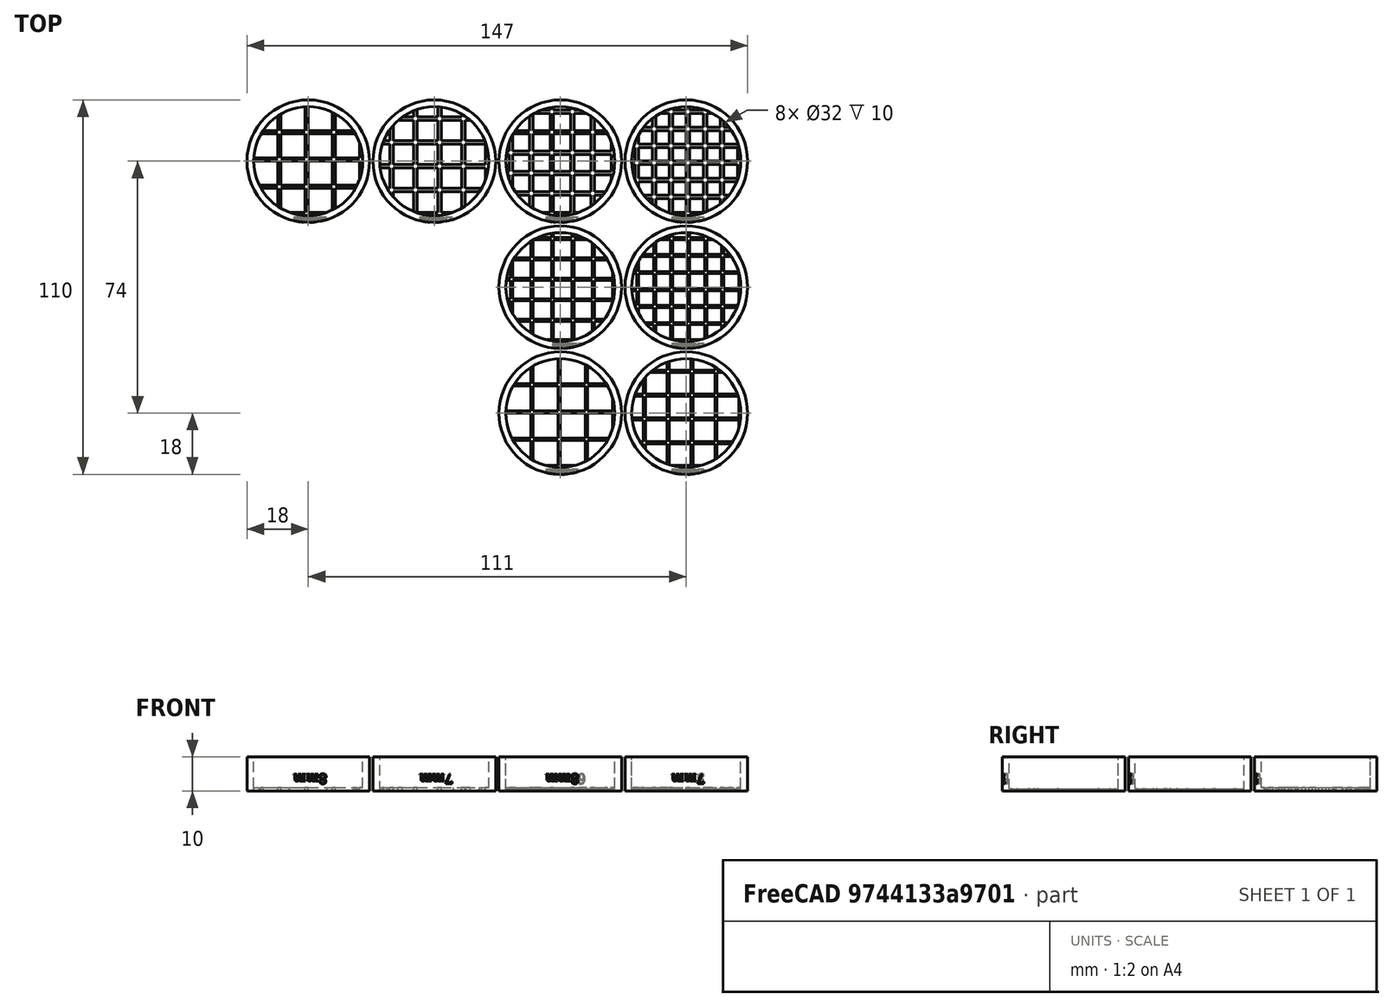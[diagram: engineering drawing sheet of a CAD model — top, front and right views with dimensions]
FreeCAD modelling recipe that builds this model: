
FCSTD DOCUMENT  (FreeCAD 0.18.4R)
Label: markingpots
License: All rights reserved
LicenseURL: http://en.wikipedia.org/wiki/All_rights_reserved
objects: Part::FeaturePython×16, Part::Cylinder×16, Part::Cut×16, Part::MultiFuse×16, Part::Box×8, Part::MultiCommon×8, Part::Part2DObjectPython×8, Part::Extrusion×8
note: 96 computed .brp shape members not serialized (recipe doc carries the construction recipe); baked Part::Feature solids carry a one-line shape summary decoded from their .brp

FEATURE [Part::Box] Box  label="Cube"
  AttacherType = Attacher::AttachEngine3D
  Height = 1
  Length = 32
  Width = 1
FEATURE [Part::FeaturePython] Array  # Draft array (typed FeaturePython)
  Angle = 360
  ArrayType = 0
  Axis = (0,0,1)
  Base = -> Box
  Center = (0,0,0)
  Fuse = false
  IntervalAxis = (0,0,0)
  IntervalX = (1,0,0)
  IntervalY = (0,5,0)
  IntervalZ = (0,0,1)
  NumberPolar = 1
  NumberX = 1
  NumberY = 7
  NumberZ = 1
FEATURE [Part::FeaturePython] Array001  # Draft array (typed FeaturePython)
  Angle = 90
  ArrayType = 1
  Axis = (0,0,1)
  Base = -> Array
  Center = (16,16,0)
  Fuse = false
  IntervalAxis = (0,0,0)
  IntervalX = (1,0,0)
  IntervalY = (0,1,0)
  IntervalZ = (0,0,1)
  NumberPolar = 2
  NumberX = 1
  NumberY = 1
  NumberZ = 1
FEATURE [Part::Cylinder] Cylinder
  Angle = 360
  AttacherType = Attacher::AttachEngine3D
  Height = 10
  Placement = pos=(16,16,0) rot=(0,0,1;0rad)
  Radius = 18
FEATURE [Part::Cylinder] Cylinder001
  Angle = 360
  AttacherType = Attacher::AttachEngine3D
  Height = 10
  Placement = pos=(16,16,0) rot=(0,0,1;0rad)
  Radius = 16
FEATURE [Part::Cut] Cut
  Base = -> Cylinder
  Tool = -> Cylinder001
FEATURE [Part::MultiFuse] Fusion
  Shapes = -> [Array001]
FEATURE [Part::MultiCommon] Common
  Shapes = -> [Cylinder,Fusion]
FEATURE [Part::MultiFuse] Fusion001
  Shapes = -> [Cut,Common]
FEATURE [Part::Part2DObjectPython] ShapeString  # Draft 2D object (typed FeaturePython)
  FontFile = <path>
  Placement = pos=(0,0,0) rot=(0,0,1;3.14159rad)
  Size = 3
  String = 5mm
  Tracking = 0
FEATURE [Part::Extrusion] Extrude
  Base = -> ShapeString
  Dir = (0,0,1)
  DirMode = 2
  FaceMakerClass = Part::FaceMakerBullseye
  LengthFwd = 2
  LengthRev = 0
  Placement = pos=(21.5,-0.5,5) rot=(1,0,0;1.5708rad)
  Solid = false
  Symmetric = false
FEATURE [Part::Cut] Cut001  label="5mm"
  Base = -> Fusion001
  Tool = -> Extrude
FEATURE [Part::Box] Box001  label="Cube001"
  AttacherType = Attacher::AttachEngine3D
  Height = 1
  Length = 32
  Width = 1
FEATURE [Part::FeaturePython] Array002  # Draft array (typed FeaturePython)
  Angle = 360
  ArrayType = 0
  Axis = (0,0,1)
  Base = -> Box001
  Center = (0,0,0)
  Fuse = false
  IntervalAxis = (0,0,0)
  IntervalX = (1,0,0)
  IntervalY = (0,6,0)
  IntervalZ = (0,0,1)
  NumberPolar = 1
  NumberX = 1
  NumberY = 7
  NumberZ = 1
FEATURE [Part::FeaturePython] Array003  # Draft array (typed FeaturePython)
  Angle = 90
  ArrayType = 1
  Axis = (0,0,1)
  Base = -> Array002
  Center = (16,16,0)
  Fuse = false
  IntervalAxis = (0,0,0)
  IntervalX = (1,0,0)
  IntervalY = (0,1,0)
  IntervalZ = (0,0,1)
  NumberPolar = 2
  NumberX = 1
  NumberY = 1
  NumberZ = 1
FEATURE [Part::Cylinder] Cylinder002
  Angle = 360
  AttacherType = Attacher::AttachEngine3D
  Height = 10
  Placement = pos=(16,16,0) rot=(0,0,1;0rad)
  Radius = 16
FEATURE [Part::MultiFuse] Fusion002
  Shapes = -> [Array003]
FEATURE [Part::Cylinder] Cylinder003
  Angle = 360
  AttacherType = Attacher::AttachEngine3D
  Height = 10
  Placement = pos=(16,16,0) rot=(0,0,1;0rad)
  Radius = 18
FEATURE [Part::MultiCommon] Common001
  Shapes = -> [Cylinder003,Fusion002]
FEATURE [Part::Cut] Cut002
  Base = -> Cylinder003
  Tool = -> Cylinder002
FEATURE [Part::MultiFuse] Fusion003
  Shapes = -> [Cut002,Common001]
FEATURE [Part::Part2DObjectPython] ShapeString001  # Draft 2D object (typed FeaturePython)
  FontFile = <path>
  Placement = pos=(0,0,0) rot=(0,0,1;3.14159rad)
  Size = 3
  String = 6mm
  Tracking = 0
FEATURE [Part::Extrusion] Extrude001
  Base = -> ShapeString001
  Dir = (0,0,1)
  DirMode = 2
  FaceMakerClass = Part::FaceMakerBullseye
  LengthFwd = 2
  LengthRev = 0
  Placement = pos=(21.5,-0.5,5) rot=(1,0,0;1.5708rad)
  Solid = false
  Symmetric = false
FEATURE [Part::Cut] Cut003  label="6mm"
  Base = -> Fusion003
  Placement = pos=(-37,0,0) rot=(0,0,1;0rad)
  Tool = -> Extrude001
FEATURE [Part::Box] Box002  label="Cube002"
  AttacherType = Attacher::AttachEngine3D
  Height = 0.6
  Length = 32
  Width = 0.6
FEATURE [Part::FeaturePython] Array004  # Draft array (typed FeaturePython)
  Angle = 360
  ArrayType = 0
  Axis = (0,0,1)
  Base = -> Box002
  Center = (0,0,0)
  Fuse = false
  IntervalAxis = (0,0,0)
  IntervalX = (1,0,0)
  IntervalY = (0,5,0)
  IntervalZ = (0,0,1)
  NumberPolar = 1
  NumberX = 1
  NumberY = 7
  NumberZ = 1
FEATURE [Part::FeaturePython] Array005  # Draft array (typed FeaturePython)
  Angle = 90
  ArrayType = 1
  Axis = (0,0,1)
  Base = -> Array004
  Center = (16,16,0)
  Fuse = false
  IntervalAxis = (0,0,0)
  IntervalX = (1,0,0)
  IntervalY = (0,1,0)
  IntervalZ = (0,0,1)
  NumberPolar = 2
  NumberX = 1
  NumberY = 1
  NumberZ = 1
FEATURE [Part::Cylinder] Cylinder004
  Angle = 360
  AttacherType = Attacher::AttachEngine3D
  Height = 10
  Placement = pos=(16,16,0) rot=(0,0,1;0rad)
  Radius = 16
FEATURE [Part::MultiFuse] Fusion004
  Shapes = -> [Array005]
FEATURE [Part::Cylinder] Cylinder005
  Angle = 360
  AttacherType = Attacher::AttachEngine3D
  Height = 10
  Placement = pos=(16,16,0) rot=(0,0,1;0rad)
  Radius = 18
FEATURE [Part::MultiCommon] Common002
  Shapes = -> [Cylinder005,Fusion004]
FEATURE [Part::Cut] Cut004
  Base = -> Cylinder005
  Tool = -> Cylinder004
FEATURE [Part::MultiFuse] Fusion005
  Shapes = -> [Cut004,Common002]
FEATURE [Part::Part2DObjectPython] ShapeString002  # Draft 2D object (typed FeaturePython)
  FontFile = <path>
  Placement = pos=(0,0,0) rot=(0,0,1;3.14159rad)
  Size = 3
  String = 5mm
  Tracking = 0
FEATURE [Part::Extrusion] Extrude002
  Base = -> ShapeString002
  Dir = (0,0,1)
  DirMode = 2
  FaceMakerClass = Part::FaceMakerBullseye
  LengthFwd = 2
  LengthRev = 0
  Placement = pos=(21.5,-0.5,5) rot=(1,0,0;1.5708rad)
  Solid = false
  Symmetric = false
FEATURE [Part::Cut] Cut005  label="5mm001"
  Base = -> Fusion005
  Placement = pos=(0,-37,0) rot=(0,0,1;0rad)
  Tool = -> Extrude002
FEATURE [Part::Part2DObjectPython] ShapeString003  # Draft 2D object (typed FeaturePython)
  FontFile = <path>
  Placement = pos=(0,0,0) rot=(0,0,1;3.14159rad)
  Size = 3
  String = 6mm
  Tracking = 0
FEATURE [Part::Cylinder] Cylinder006
  Angle = 360
  AttacherType = Attacher::AttachEngine3D
  Height = 10
  Placement = pos=(16,16,0) rot=(0,0,1;0rad)
  Radius = 16
FEATURE [Part::Cylinder] Cylinder007
  Angle = 360
  AttacherType = Attacher::AttachEngine3D
  Height = 10
  Placement = pos=(16,16,0) rot=(0,0,1;0rad)
  Radius = 18
FEATURE [Part::Box] Box003  label="Cube003"
  AttacherType = Attacher::AttachEngine3D
  Height = 0.6
  Length = 32
  Width = 0.6
FEATURE [Part::Extrusion] Extrude003
  Base = -> ShapeString003
  Dir = (0,0,1)
  DirMode = 2
  FaceMakerClass = Part::FaceMakerBullseye
  LengthFwd = 2
  LengthRev = 0
  Placement = pos=(23.5,-0.5,5) rot=(1,0,0;1.5708rad)
  Solid = false
  Symmetric = false
FEATURE [Part::Cut] Cut007
  Base = -> Cylinder007
  Tool = -> Cylinder006
FEATURE [Part::FeaturePython] Array007  # Draft array (typed FeaturePython)
  Angle = 360
  ArrayType = 0
  Axis = (0,0,1)
  Base = -> Box003
  Center = (0,0,0)
  Fuse = false
  IntervalAxis = (0,0,0)
  IntervalX = (1,0,0)
  IntervalY = (0,6,0)
  IntervalZ = (0,0,1)
  NumberPolar = 1
  NumberX = 1
  NumberY = 7
  NumberZ = 1
FEATURE [Part::FeaturePython] Array006  # Draft array (typed FeaturePython)
  Angle = 90
  ArrayType = 1
  Axis = (0,0,1)
  Base = -> Array007
  Center = (16,16,0)
  Fuse = false
  IntervalAxis = (0,0,0)
  IntervalX = (1,0,0)
  IntervalY = (0,1,0)
  IntervalZ = (0,0,1)
  NumberPolar = 2
  NumberX = 1
  NumberY = 1
  NumberZ = 1
FEATURE [Part::MultiFuse] Fusion007
  Shapes = -> [Array006]
FEATURE [Part::MultiCommon] Common003
  Shapes = -> [Cylinder007,Fusion007]
FEATURE [Part::MultiFuse] Fusion006
  Shapes = -> [Cut007,Common003]
FEATURE [Part::Cut] Cut006  label="6mm001"
  Base = -> Fusion006
  Placement = pos=(-37,-37,0) rot=(0,0,1;0rad)
  Tool = -> Extrude003
FEATURE [Part::Part2DObjectPython] ShapeString004  # Draft 2D object (typed FeaturePython)
  FontFile = <path>
  Placement = pos=(0,0,0) rot=(0,0,1;3.14159rad)
  Size = 3
  String = 7mm
  Tracking = 0
FEATURE [Part::Cylinder] Cylinder008
  Angle = 360
  AttacherType = Attacher::AttachEngine3D
  Height = 10
  Placement = pos=(16,16,0) rot=(0,0,1;0rad)
  Radius = 16
FEATURE [Part::Cylinder] Cylinder009
  Angle = 360
  AttacherType = Attacher::AttachEngine3D
  Height = 10
  Placement = pos=(16,16,0) rot=(0,0,1;0rad)
  Radius = 18
FEATURE [Part::Box] Box004  label="Cube004"
  AttacherType = Attacher::AttachEngine3D
  Height = 1
  Length = 32
  Width = 1
FEATURE [Part::Extrusion] Extrude004
  Base = -> ShapeString004
  Dir = (0,0,1)
  DirMode = 2
  FaceMakerClass = Part::FaceMakerBullseye
  LengthFwd = 2
  LengthRev = 0
  Placement = pos=(21.5,-0.5,5) rot=(1,0,0;1.5708rad)
  Solid = false
  Symmetric = false
FEATURE [Part::Cut] Cut011
  Base = -> Cylinder009
  Tool = -> Cylinder008
FEATURE [Part::FeaturePython] Array011  # Draft array (typed FeaturePython)
  Angle = 360
  ArrayType = 0
  Axis = (0,0,1)
  Base = -> Box004
  Center = (0,0,0)
  Fuse = false
  IntervalAxis = (0,0,0)
  IntervalX = (1,0,0)
  IntervalY = (0,7,0)
  IntervalZ = (0,0,1)
  NumberPolar = 1
  NumberX = 1
  NumberY = 7
  NumberZ = 1
FEATURE [Part::FeaturePython] Array008  # Draft array (typed FeaturePython)
  Angle = 90
  ArrayType = 1
  Axis = (0,0,1)
  Base = -> Array011
  Center = (16,16,0)
  Fuse = false
  IntervalAxis = (0,0,0)
  IntervalX = (1,0,0)
  IntervalY = (0,1,0)
  IntervalZ = (0,0,1)
  NumberPolar = 2
  NumberX = 1
  NumberY = 1
  NumberZ = 1
FEATURE [Part::MultiFuse] Fusion011
  Shapes = -> [Array008]
FEATURE [Part::MultiCommon] Common004
  Shapes = -> [Cylinder009,Fusion011]
FEATURE [Part::MultiFuse] Fusion009
  Shapes = -> [Cut011,Common004]
FEATURE [Part::Cut] Cut008  label="7mm"
  Base = -> Fusion009
  Placement = pos=(-74,0,0) rot=(0,0,1;0rad)
  Tool = -> Extrude004
FEATURE [Part::Part2DObjectPython] ShapeString005  # Draft 2D object (typed FeaturePython)
  FontFile = <path>
  Placement = pos=(0,0,0) rot=(0,0,1;3.14159rad)
  Size = 3
  String = 7mm
  Tracking = 0
FEATURE [Part::Extrusion] Extrude005
  Base = -> ShapeString005
  Dir = (0,0,1)
  DirMode = 2
  FaceMakerClass = Part::FaceMakerBullseye
  LengthFwd = 2
  LengthRev = 0
  Placement = pos=(21.5,-0.5,5) rot=(1,0,0;1.5708rad)
  Solid = false
  Symmetric = false
FEATURE [Part::Cylinder] Cylinder010
  Angle = 360
  AttacherType = Attacher::AttachEngine3D
  Height = 10
  Placement = pos=(16,16,0) rot=(0,0,1;0rad)
  Radius = 16
FEATURE [Part::Box] Box005  label="Cube005"
  AttacherType = Attacher::AttachEngine3D
  Height = 0.6
  Length = 32
  Width = 0.6
FEATURE [Part::Cylinder] Cylinder011
  Angle = 360
  AttacherType = Attacher::AttachEngine3D
  Height = 10
  Placement = pos=(16,16,0) rot=(0,0,1;0rad)
  Radius = 18
FEATURE [Part::Cut] Cut012
  Base = -> Cylinder011
  Tool = -> Cylinder010
FEATURE [Part::FeaturePython] Array013  # Draft array (typed FeaturePython)
  Angle = 360
  ArrayType = 0
  Axis = (0,0,1)
  Base = -> Box005
  Center = (0,0,0)
  Fuse = false
  IntervalAxis = (0,0,0)
  IntervalX = (1,0,0)
  IntervalY = (0,7,0)
  IntervalZ = (0,0,1)
  NumberPolar = 1
  NumberX = 1
  NumberY = 7
  NumberZ = 1
FEATURE [Part::FeaturePython] Array012  # Draft array (typed FeaturePython)
  Angle = 90
  ArrayType = 1
  Axis = (0,0,1)
  Base = -> Array013
  Center = (16,16,0)
  Fuse = false
  IntervalAxis = (0,0,0)
  IntervalX = (1,0,0)
  IntervalY = (0,1,0)
  IntervalZ = (0,0,1)
  NumberPolar = 2
  NumberX = 1
  NumberY = 1
  NumberZ = 1
FEATURE [Part::MultiFuse] Fusion012
  Shapes = -> [Array012]
FEATURE [Part::MultiCommon] Common005
  Shapes = -> [Cylinder011,Fusion012]
FEATURE [Part::MultiFuse] Fusion013
  Shapes = -> [Cut012,Common005]
FEATURE [Part::Cut] Cut013  label="7mm001"
  Base = -> Fusion013
  Placement = pos=(0,-74,0) rot=(0,0,1;0rad)
  Tool = -> Extrude005
FEATURE [Part::Part2DObjectPython] ShapeString006  # Draft 2D object (typed FeaturePython)
  FontFile = <path>
  Placement = pos=(0,0,0) rot=(0,0,1;3.14159rad)
  Size = 3
  String = 8mm
  Tracking = 0
FEATURE [Part::Cylinder] Cylinder012
  Angle = 360
  AttacherType = Attacher::AttachEngine3D
  Height = 10
  Placement = pos=(16,16,0) rot=(0,0,1;0rad)
  Radius = 16
FEATURE [Part::Cylinder] Cylinder013
  Angle = 360
  AttacherType = Attacher::AttachEngine3D
  Height = 10
  Placement = pos=(16,16,0) rot=(0,0,1;0rad)
  Radius = 18
FEATURE [Part::Box] Box006  label="Cube006"
  AttacherType = Attacher::AttachEngine3D
  Height = 1
  Length = 32
  Width = 1
FEATURE [Part::Extrusion] Extrude006
  Base = -> ShapeString006
  Dir = (0,0,1)
  DirMode = 2
  FaceMakerClass = Part::FaceMakerBullseye
  LengthFwd = 2
  LengthRev = 0
  Placement = pos=(21.5,-0.5,5) rot=(1,0,0;1.5708rad)
  Solid = false
  Symmetric = false
FEATURE [Part::Cut] Cut015
  Base = -> Cylinder013
  Tool = -> Cylinder012
FEATURE [Part::FeaturePython] Array015  # Draft array (typed FeaturePython)
  Angle = 360
  ArrayType = 0
  Axis = (0,0,1)
  Base = -> Box006
  Center = (0,0,0)
  Fuse = false
  IntervalAxis = (0,0,0)
  IntervalX = (1,0,0)
  IntervalY = (0,8,0)
  IntervalZ = (0,0,1)
  NumberPolar = 1
  NumberX = 1
  NumberY = 7
  NumberZ = 1
FEATURE [Part::FeaturePython] Array014  # Draft array (typed FeaturePython)
  Angle = 90
  ArrayType = 1
  Axis = (0,0,1)
  Base = -> Array015
  Center = (16,16,0)
  Fuse = false
  IntervalAxis = (0,0,0)
  IntervalX = (1,0,0)
  IntervalY = (0,1,0)
  IntervalZ = (0,0,1)
  NumberPolar = 2
  NumberX = 1
  NumberY = 1
  NumberZ = 1
FEATURE [Part::MultiFuse] Fusion015
  Shapes = -> [Array014]
FEATURE [Part::MultiCommon] Common006
  Shapes = -> [Cylinder013,Fusion015]
FEATURE [Part::MultiFuse] Fusion014
  Shapes = -> [Cut015,Common006]
FEATURE [Part::Cut] Cut014  label="8mm"
  Base = -> Fusion014
  Placement = pos=(-111,0,0) rot=(0,0,1;0rad)
  Tool = -> Extrude006
FEATURE [Part::Part2DObjectPython] ShapeString007  # Draft 2D object (typed FeaturePython)
  FontFile = <path>
  Placement = pos=(0,0,0) rot=(0,0,1;3.14159rad)
  Size = 3
  String = 8mm
  Tracking = 0
FEATURE [Part::Extrusion] Extrude007
  Base = -> ShapeString007
  Dir = (0,0,1)
  DirMode = 2
  FaceMakerClass = Part::FaceMakerBullseye
  LengthFwd = 2
  LengthRev = 0
  Placement = pos=(21.5,-0.5,5) rot=(1,0,0;1.5708rad)
  Solid = false
  Symmetric = false
FEATURE [Part::Cylinder] Cylinder014
  Angle = 360
  AttacherType = Attacher::AttachEngine3D
  Height = 10
  Placement = pos=(16,16,0) rot=(0,0,1;0rad)
  Radius = 16
FEATURE [Part::Box] Box007  label="Cube007"
  AttacherType = Attacher::AttachEngine3D
  Height = 0.6
  Length = 32
  Width = 0.6
FEATURE [Part::Cylinder] Cylinder015
  Angle = 360
  AttacherType = Attacher::AttachEngine3D
  Height = 10
  Placement = pos=(16,16,0) rot=(0,0,1;0rad)
  Radius = 18
FEATURE [Part::Cut] Cut016
  Base = -> Cylinder015
  Tool = -> Cylinder014
FEATURE [Part::FeaturePython] Array017  # Draft array (typed FeaturePython)
  Angle = 360
  ArrayType = 0
  Axis = (0,0,1)
  Base = -> Box007
  Center = (0,0,0)
  Fuse = false
  IntervalAxis = (0,0,0)
  IntervalX = (1,0,0)
  IntervalY = (0,8,0)
  IntervalZ = (0,0,1)
  NumberPolar = 1
  NumberX = 1
  NumberY = 7
  NumberZ = 1
FEATURE [Part::FeaturePython] Array016  # Draft array (typed FeaturePython)
  Angle = 90
  ArrayType = 1
  Axis = (0,0,1)
  Base = -> Array017
  Center = (16,16,0)
  Fuse = false
  IntervalAxis = (0,0,0)
  IntervalX = (1,0,0)
  IntervalY = (0,1,0)
  IntervalZ = (0,0,1)
  NumberPolar = 2
  NumberX = 1
  NumberY = 1
  NumberZ = 1
FEATURE [Part::MultiFuse] Fusion016
  Shapes = -> [Array016]
FEATURE [Part::MultiCommon] Common007
  Shapes = -> [Cylinder015,Fusion016]
FEATURE [Part::MultiFuse] Fusion017
  Shapes = -> [Cut016,Common007]
FEATURE [Part::Cut] Cut017  label="8mm001"
  Base = -> Fusion017
  Placement = pos=(-37,-74,0) rot=(0,0,1;0rad)
  Tool = -> Extrude007
note: 8 file-system paths scrubbed to <path> (originals preserved in the JSON sidecar)
